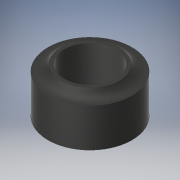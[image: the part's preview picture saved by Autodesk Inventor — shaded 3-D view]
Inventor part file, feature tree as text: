
AUTODESK INVENTOR PART (.ipt)
format: ipt  version: 2019 (Build 230136000, 136)  size: 123,392 bytes
history: native  units: mm
features: extrude x2, sketch x2, fillet x1
ambient origin geometry x8: Origin, YZ Plane, XZ Plane, XY Plane, X Axis, Y Axis, Z Axis, Center Point
bodies: Solid1 (feature_tree)
feature tree (5):
  extrude  "Extrusion1"  Depth=8.0mm
  extrude  "Extrusion2"  Depth=1.0mm TaperAngle=0.0deg
  fillet  "Fillet1"  Radius=2.0mm
  sketch  "Sketch1"  dims[d0=13.0mm d1=8.0mm]
  sketch  "Sketch2"  dims[d2=7.0mm d3=0.0mm d4=1.0mm d5=0.0mm d6=2.0mm]
